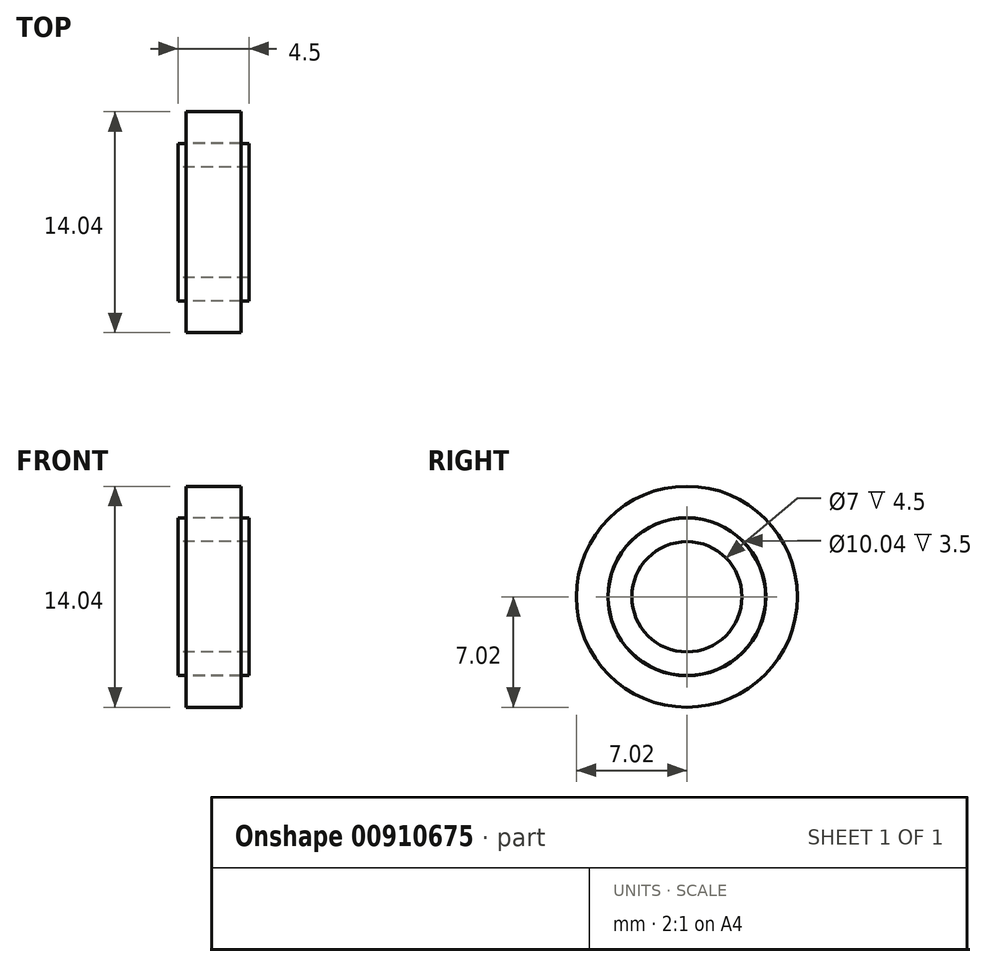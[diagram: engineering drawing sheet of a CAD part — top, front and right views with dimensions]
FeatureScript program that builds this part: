
annotation { "Feature Type Name" : "Feature", "Feature Type Description" : "" }
export const myFeature = defineFeature(function(context is Context, id is Id, definition is map)
    precondition{}
    {
        {
            var Q0;
            Q0=qCreatedBy(makeId("Top.planeOp"),FACE);
            var sketch = newSketch(context, id + "F0", { "sketchPlane" : qUnion([Q0])});
            skLineSegment(sketch, "E0", {"start": v(0, 0) * mm, "end": v(0, 3.5) * mm});
            skLineSegment(sketch, "E1.top", {"start": v(0, 5) * mm, "end": v(4.5, 5) * mm});
            skLineSegment(sketch, "E1.left", {"start": v(0, 3.5) * mm, "end": v(0, 5) * mm});
            skLineSegment(sketch, "E1.right", {"start": v(4.5, 3.5) * mm, "end": v(4.5, 5) * mm});
            skLineSegment(sketch, "E2", {"start": v(0, 3.5) * mm, "end": v(4.5, 3.5) * mm});
            skLineSegment(sketch, "E3", {"start": v(0, 0) * mm, "end": v(4.5, 0) * mm});
            skSolve(sketch);
        }
        {
            var Q0;
            Q0=qCreatedBy(makeId("Top.planeOp"),FACE);
            var sketch = newSketch(context, id + "F1", { "sketchPlane" : qUnion([Q0])});
            skLineSegment(sketch, "E4", {"start": v(0, 5.02) * mm, "end": v(0.5, 5.02) * mm});
            skLineSegment(sketch, "E5", {"start": v(0.5, 5.02) * mm, "end": v(0.5, 7.02) * mm});
            skLineSegment(sketch, "E6", {"start": v(0.5, 7.02) * mm, "end": v(4, 7.02) * mm});
            skLineSegment(sketch, "E7", {"start": v(4, 7.02) * mm, "end": v(4, 5.02) * mm});
            skLineSegment(sketch, "E8", {"start": v(4, 5.02) * mm, "end": v(0.5, 5.02) * mm});
            skSolve(sketch);
        }
        {
            var Q0;
            Q0 = qSketchRegion(id + "F0", true);
            var Q1;
            Q1=sQuery(id+"F0.wireOp",EDGE,"E3");
            revolve(context, id + "F2", {"surfaceOperationType" : NewSurfaceOperationType.NEW, "entities" : qUnion([Q0]), "axis" : qUnion([Q1]), "revolveType" : RevolveType.FULL});
        }
        {
            var Q0;
            Q0 = qSketchRegion(id + "F1", true);
            var Q1;
            Q1=sQuery(id+"F0.wireOp",EDGE,"E3");
            revolve(context, id + "F3", {"surfaceOperationType" : NewSurfaceOperationType.NEW, "entities" : qUnion([Q0]), "axis" : qUnion([Q1]), "revolveType" : RevolveType.FULL});
        }
    });
